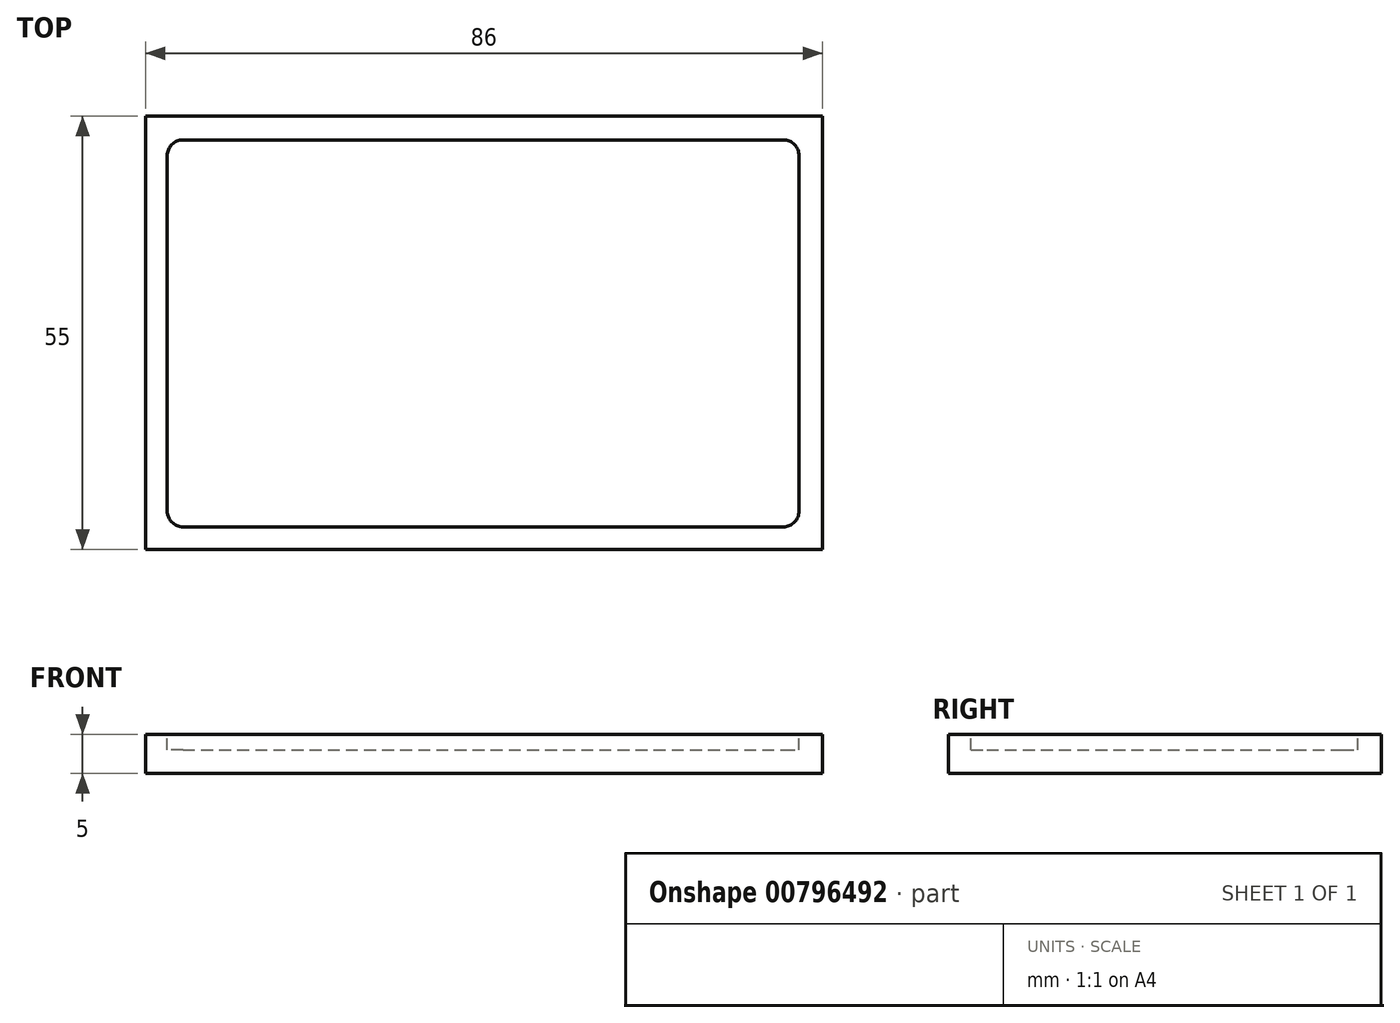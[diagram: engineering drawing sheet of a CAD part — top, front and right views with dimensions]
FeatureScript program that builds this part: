
annotation { "Feature Type Name" : "Feature", "Feature Type Description" : "" }
export const myFeature = defineFeature(function(context is Context, id is Id, definition is map)
    precondition{}
    {
        {
            var Q0;
            Q0=qCreatedBy(makeId("Top.planeOp"),FACE);
            var sketch = newSketch(context, id + "F0", { "sketchPlane" : qUnion([Q0])});
            skLineSegment(sketch, "E0", {"start": v(-43, 27.5) * mm, "end": v(43, 27.5) * mm});
            skLineSegment(sketch, "E1", {"start": v(43, 27.5) * mm, "end": v(43, -27.5) * mm});
            skLineSegment(sketch, "E2", {"start": v(43, -27.5) * mm, "end": v(-43, -27.5) * mm});
            skLineSegment(sketch, "E3", {"start": v(-43, -27.5) * mm, "end": v(-43, 27.5) * mm});
            skPoint(sketch, "E4.endSnap0", {"position": v(-43, 0) * mm});
            skSolve(sketch);
        }
        {
            var Q0;
            Q0=makeQuery(id+"F0.imprint","IMPRINT",FACE,{"disambiguationData":[TD([[makeQuery(id+"F0.imprint","IMPRINT",EDGE,{"derivedFrom":sQuery(id+"F0.wireOp",EDGE,"E0")}),-1.0]])]});
            extrude(context, id + "F1", {"entities" : qUnion([Q0]), "depth" : 5 * mm, "offsetDistance" : 25 * mm});
        }
        {
            var Q0;
            Q0=makeQuery(id+"F1.opExtrude","CAP_FACE",FACE,{"disambiguationData":[OSD([sQuery(id+"F0.wireOp",EDGE,"E0"),sQuery(id+"F0.wireOp",EDGE,"E1"),sQuery(id+"F0.wireOp",EDGE,"E2"),sQuery(id+"F0.wireOp",EDGE,"E3")])],"isStart":false});
            var sketch = newSketch(context, id + "F2", { "sketchPlane" : qUnion([Q0])});
            skLineSegment(sketch, "E5", {"start": v(-40.25, 24.5) * mm, "end": v(40, 24.5) * mm});
            skLineSegment(sketch, "E6", {"start": v(40, 24.5) * mm, "end": v(40, -24.65) * mm});
            skLineSegment(sketch, "E7", {"start": v(40, -24.65) * mm, "end": v(-40.25, -24.65) * mm});
            skLineSegment(sketch, "E8", {"start": v(-40.25, -24.65) * mm, "end": v(-40.25, 24.5) * mm});
            skSolve(sketch);
        }
        {
            var Q0;
            Q0=makeQuery(id+"F2.imprint","IMPRINT",FACE,{"disambiguationData":[TD([[makeQuery(id+"F2.imprint","IMPRINT",EDGE,{"derivedFrom":sQuery(id+"F2.wireOp",EDGE,"E5")}),-1.0]])]});
            extrude(context, id + "F3", {"entities" : qUnion([Q0]), "operationType" : NewBodyOperationType.REMOVE, "oppositeDirection" : true, "depth" : 2 * mm, "offsetDistance" : 25 * mm});
        }
        {
            var Q0;
            Q0=makeQuery(id+"F3.boolean.opBoolean","COPY",EDGE,{"derivedFrom":makeQuery(id+"F3.opExtrude","SWEPT_EDGE",EDGE,{"disambiguationData":[OSD([sQuery(id+"F2.wireOp",EDGE,"E5"),sQuery(id+"F2.wireOp",EDGE,"E8")])]})});
            var Q1;
            Q1=makeQuery(id+"F3.boolean.opBoolean","COPY",EDGE,{"derivedFrom":makeQuery(id+"F3.opExtrude","SWEPT_EDGE",EDGE,{"disambiguationData":[OSD([sQuery(id+"F2.wireOp",EDGE,"E7"),sQuery(id+"F2.wireOp",EDGE,"E8")])]})});
            var Q2;
            Q2=makeQuery(id+"F3.boolean.opBoolean","COPY",EDGE,{"derivedFrom":makeQuery(id+"F3.opExtrude","SWEPT_EDGE",EDGE,{"disambiguationData":[OSD([sQuery(id+"F2.wireOp",EDGE,"E5"),sQuery(id+"F2.wireOp",EDGE,"E6")])]})});
            var Q3;
            Q3=makeQuery(id+"F3.boolean.opBoolean","COPY",EDGE,{"derivedFrom":makeQuery(id+"F3.opExtrude","SWEPT_EDGE",EDGE,{"disambiguationData":[OSD([sQuery(id+"F2.wireOp",EDGE,"E6"),sQuery(id+"F2.wireOp",EDGE,"E7")])]})});
            fillet(context, id + "F4", {"entities" : qUnion([Q0, Q1, Q2, Q3]), "radius" : 2 * mm, "tangentPropagation" : true, "allowEdgeOverflow" : false});
        }
    });
